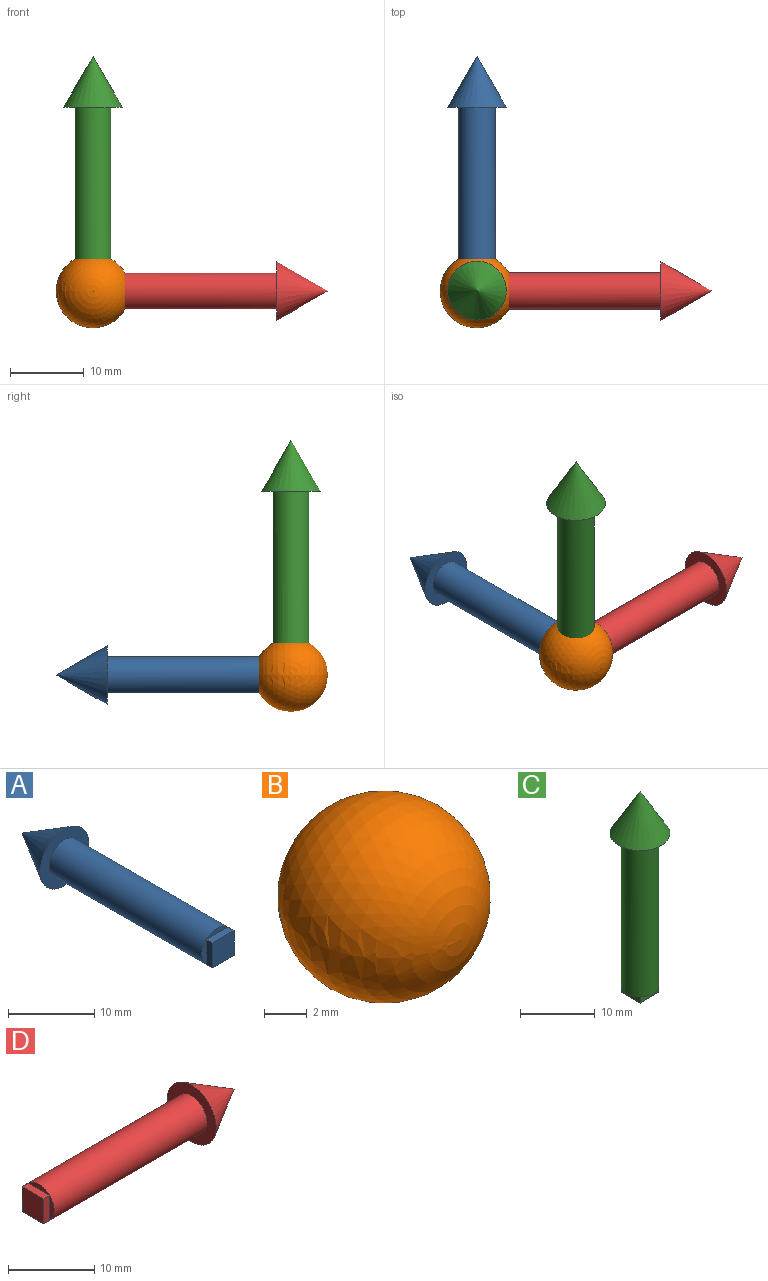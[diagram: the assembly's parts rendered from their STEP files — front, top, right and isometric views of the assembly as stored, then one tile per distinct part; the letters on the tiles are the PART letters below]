
ASSEMBLY  parts=4 mates=7
PART A: 12 faces, bbox 8x32.9x8 mm
  f0: plane 3.54x0.73mm, normal (0,-1,0), area 1.8mm2, adj f3,f7
  f1: plane 3.54x0.73mm, normal (0,-1,0), area 1.8mm2, adj f3,f10
  f2: plane 3.54x0.73mm, normal (0,-1,0), area 1.8mm2, adj f3,f9
  f3: cylinder r=2.5mm len=25mm, axis (0,-1,0), area 392.7mm2, adj f0,f1,f2,f4,f6
  f4: plane 3.54x0.73mm, normal (0,-1,0), area 1.8mm2, adj f3,f8
  f5: cone r=4mm half-angle=30deg, axis (0,-1,0), area 100.5mm2, adj f6
  f6: plane 8x8mm, normal (0,-1,0), area 30.6mm2, adj f3,f5
  f7: plane 3.54x1mm, normal (0,0,1), area 3.5mm2, adj f0,f8,f10,f11
  f8: plane 3.54x1mm, normal (-1,0,0), area 3.5mm2, adj f4,f7,f9,f11
  f9: plane 3.54x1mm, normal (0,0,-1), area 3.5mm2, adj f2,f8,f10,f11
  f10: plane 3.54x1mm, normal (1,0,0), area 3.5mm2, adj f1,f7,f9,f11
  f11: plane 3.54x3.54mm, normal (0,-1,0), area 12.5mm2, adj f7,f8,f9,f10
PART B: 2 faces, bbox 10x10x10 mm
  f0: sphere r=5mm, area 314.2mm2
  f1: sphere r=2.5mm, area 78.5mm2
PART C: 12 faces, bbox 8x8x32.9 mm
  f0: plane 3.54x0.73mm, normal (0,0,-1), area 1.8mm2, adj f3,f7
  f1: plane 3.54x0.73mm, normal (0,0,-1), area 1.8mm2, adj f3,f9
  f2: plane 3.54x0.73mm, normal (0,0,-1), area 1.8mm2, adj f3,f8
  f3: cylinder r=2.5mm len=25mm, axis (0,0,-1), area 392.7mm2, adj f0,f1,f2,f4,f6
  f4: plane 3.54x0.73mm, normal (0,0,-1), area 1.8mm2, adj f3,f10
  f5: cone r=4mm half-angle=30deg, axis (0,0,-1), area 100.5mm2, adj f6
  f6: plane 8x8mm, normal (0,0,-1), area 30.6mm2, adj f3,f5
  f7: plane 3.54x1mm, normal (-1,0,0), area 3.5mm2, adj f0,f8,f10,f11
  f8: plane 3.54x1mm, normal (0,1,0), area 3.5mm2, adj f2,f7,f9,f11
  f9: plane 3.54x1mm, normal (1,0,0), area 3.5mm2, adj f1,f8,f10,f11
  f10: plane 3.54x1mm, normal (0,-1,0), area 3.5mm2, adj f4,f7,f9,f11
  f11: plane 3.54x3.54mm, normal (0,0,-1), area 12.5mm2, adj f7,f8,f9,f10
PART D: 12 faces, bbox 32.9x8x8 mm
  f0: plane 3.54x0.73mm, normal (-1,0,0), area 1.8mm2, adj f3,f7
  f1: plane 3.54x0.73mm, normal (-1,0,0), area 1.8mm2, adj f3,f9
  f2: plane 3.54x0.73mm, normal (-1,0,0), area 1.8mm2, adj f3,f8
  f3: cylinder r=2.5mm len=25mm, axis (-1,0,0), area 392.7mm2, adj f0,f1,f2,f4,f6
  f4: plane 3.54x0.73mm, normal (-1,0,0), area 1.8mm2, adj f3,f10
  f5: cone r=4mm half-angle=30deg, axis (-1,0,0), area 100.5mm2, adj f6
  f6: plane 8x8mm, normal (-1,0,0), area 30.6mm2, adj f3,f5
  f7: plane 3.54x1mm, normal (0,0,1), area 3.5mm2, adj f0,f8,f10,f11
  f8: plane 3.54x1mm, normal (0,1,0), area 3.5mm2, adj f2,f7,f9,f11
  f9: plane 3.54x1mm, normal (0,0,-1), area 3.5mm2, adj f1,f8,f10,f11
  f10: plane 3.54x1mm, normal (0,-1,0), area 3.5mm2, adj f4,f7,f9,f11
  f11: plane 3.54x3.54mm, normal (-1,0,0), area 12.5mm2, adj f7,f8,f9,f10
PLACE A at identity
PLACE B at identity
PLACE C at identity
PLACE D rot(axis=(-1,0,0),90deg) t=(0,0,0)mm
MATE parallel D.f10 <-> C.f5  axis (0,0,1) through (-0.5,0,1.77)mm
MATE ball D.f3 <-> B.f0  axis (-1,0,0) through (0,0,0)mm
MATE fastened C.f3 <-> B.f0  axis (0,0,-1) through (0,0,0)mm
MATE ball A.f3 <-> B.f0  axis (0,-1,0) through (0,0,0)mm
MATE parallel A.f7 <-> C.f5  axis (0,0,1) through (0,-0.5,1.77)mm
MATE parallel C.f7 <-> A.f8  axis (-1,0,0) through (-1.77,0,-0.5)mm
MATE parallel D.f9 <-> A.f3  axis (0,-1,0) through (-0.5,-1.77,0)mm
